# Revit family: Furniture-Medicine_Cabinet-KOHLER-Archer-K-3073
name_source: partatom
category: Specialty Equipment
revit_build: Autodesk Revit 2015 (Build: 20140606_1530(x64)
units: mm (PartAtom-declared; Revit-internal decimal feet)

## types (1)
- NA-Anodized Aluminium
    ADA Compliant = No
    Assembly Code = C1030200
    Date Modified = 02/07/2019
    Default Elevation = 60"
    Description = 20 inch W x 31 inch H aluminum single-door medicine cabinet, beveled edges
    Finish = Kohler-Metal-NA-Anodized_Aluminum
    Height = 31"
    Manufacturer = KOHLER Co.
    MasterFormat 1995 = 10820
    MasterFormat 2004 = 10.28.13
    Material = Anodized Aluminum
    Model = K-3073-NA
    Product Documentation Link = https://www.us.kohler.com
    Product Name = Archer
    Product Page URL = http://www.us.kohler.com
    URL = https://www.us.kohler.com
    WaterSense Certified = No
    Width = 20"

## geometry (parser evidence)
native form markers: Sweep x4
no freeform markers — native parametric forms only
